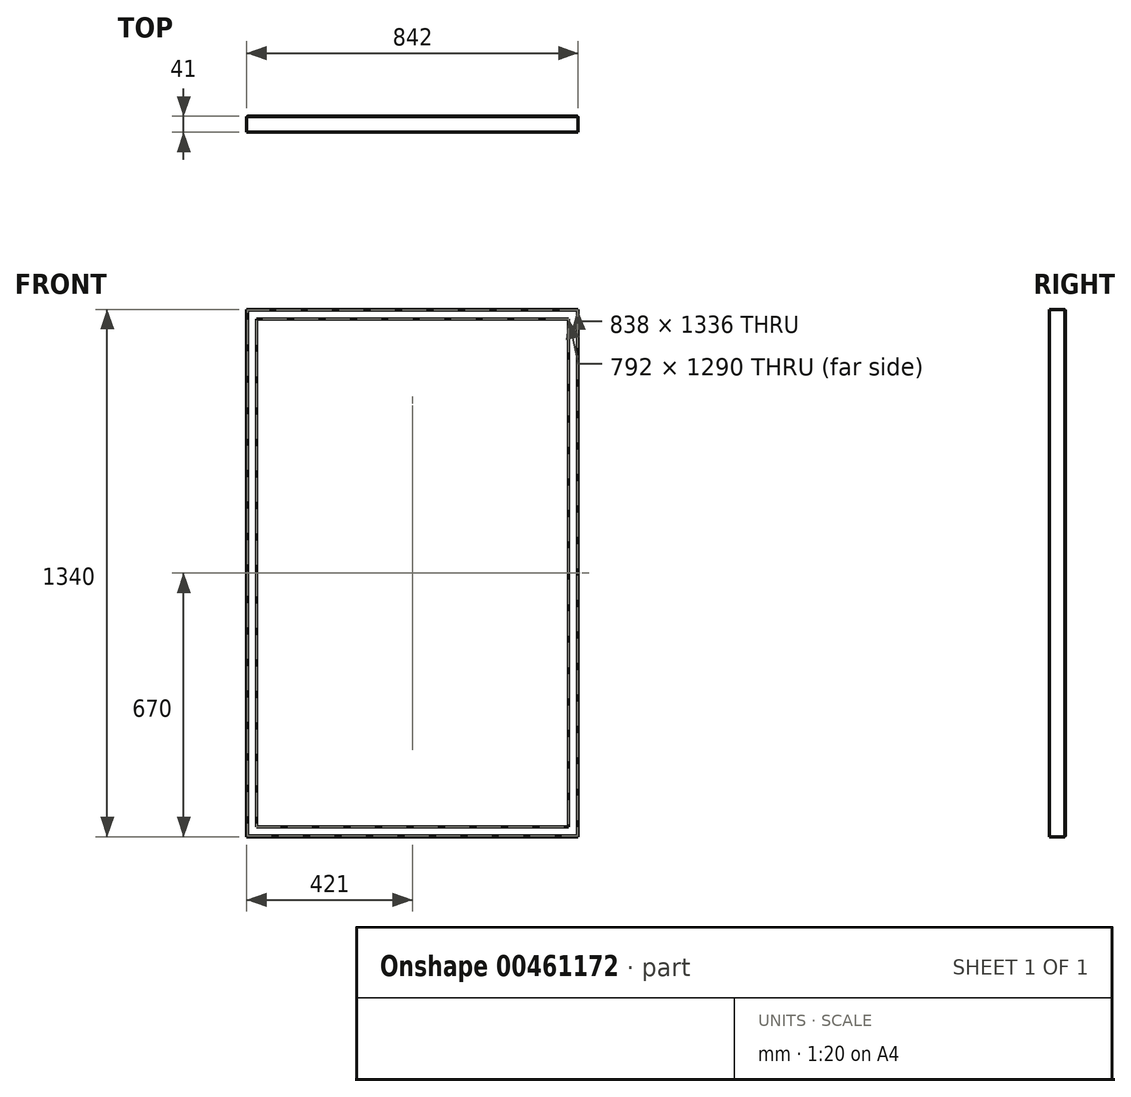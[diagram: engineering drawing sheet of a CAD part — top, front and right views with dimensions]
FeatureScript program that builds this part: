
annotation { "Feature Type Name" : "Feature", "Feature Type Description" : "" }
export const myFeature = defineFeature(function(context is Context, id is Id, definition is map)
    precondition{}
    {
        {
            var Q0;
            Q0=qCreatedBy(makeId("Front.planeOp"),FACE);
            var sketch = newSketch(context, id + "F0", { "sketchPlane" : qUnion([Q0])});
            skLineSegment(sketch, "E0.bottom", {"start": v(419, -668) * mm, "end": v(-419, -668) * mm});
            skLineSegment(sketch, "E0.top", {"start": v(419, 668) * mm, "end": v(-419, 668) * mm});
            skLineSegment(sketch, "E0.left", {"start": v(419, -668) * mm, "end": v(419, 668) * mm});
            skLineSegment(sketch, "E0.right", {"start": v(-419, -668) * mm, "end": v(-419, 668) * mm});
            skPoint(sketch, "E0.middle", {"position": v(0, 0) * mm});
            skLineSegment(sketch, "E1.0", {"start": v(-396, -645) * mm, "end": v(-396, 645) * mm});
            skLineSegment(sketch, "E2.0", {"start": v(396, -645) * mm, "end": v(396, 645) * mm});
            skLineSegment(sketch, "E3.0", {"start": v(396, -645) * mm, "end": v(-396, -645) * mm});
            skLineSegment(sketch, "E4.0", {"start": v(396, 645) * mm, "end": v(-396, 645) * mm});
            skSolve(sketch);
        }
        {
            var Q0;
            Q0 = qSketchRegion(id + "F0", true);
            extrude(context, id + "F1", {"entities" : qUnion([Q0]), "endBound" : BoundingType.SYMMETRIC, "depth" : 2 * mm});
        }
        {
            var Q0;
            Q0=makeQuery(id+"F0.imprint","IMPRINT",FACE,{"disambiguationData":[TD([[makeQuery(id+"F0.imprint","IMPRINT",EDGE,{"derivedFrom":sQuery(id+"F0.wireOp",EDGE,"E0.bottom")}),-1.0]])]});
            var sketch = newSketch(context, id + "F2", { "sketchPlane" : qUnion([Q0])});
            skLineSegment(sketch, "E5.bottom", {"start": v(421, -670) * mm, "end": v(-421, -670) * mm});
            skLineSegment(sketch, "E5.top", {"start": v(421, 670) * mm, "end": v(-421, 670) * mm});
            skLineSegment(sketch, "E5.left", {"start": v(421, -670) * mm, "end": v(421, 670) * mm});
            skLineSegment(sketch, "E5.right", {"start": v(-421, -670) * mm, "end": v(-421, 670) * mm});
            skPoint(sketch, "E5.middle", {"position": v(0, 0) * mm});
            skLineSegment(sketch, "E6.0", {"start": v(-419, -668) * mm, "end": v(-419, 668) * mm});
            skLineSegment(sketch, "E7.0", {"start": v(419, 668) * mm, "end": v(-419, 668) * mm});
            skLineSegment(sketch, "E8.0.0", {"start": v(419, -668) * mm, "end": v(419, 668) * mm});
            skLineSegment(sketch, "E8.0.2", {"start": v(-419, 668) * mm, "end": v(-419, -668) * mm});
            skLineSegment(sketch, "E8.0.3", {"start": v(-419, -668) * mm, "end": v(419, -668) * mm});
            skSolve(sketch);
        }
        {
            var Q0;
            Q0 = qSketchRegion(id + "F2", true);
            extrude(context, id + "F3", {"entities" : qUnion([Q0]), "depth" : 40 * mm});
        }
    });
